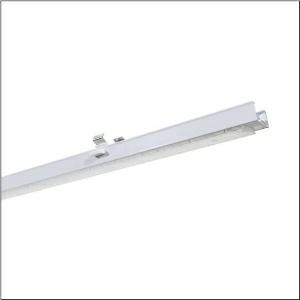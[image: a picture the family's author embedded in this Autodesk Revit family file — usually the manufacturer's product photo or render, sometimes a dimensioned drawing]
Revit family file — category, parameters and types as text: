
# Revit family: trunking_flex_31_51re12ma16b
name_source: partatom
category: Lighting Fixtures
units: mm (PartAtom-declared; Revit-internal decimal feet)

## family parameters
Cut with Voids When Loaded = No
Host = Face
Light Source = No
Part Type = Normal
Room Calculation Point = No
Round Connector Dimension = Use Diameter
Shared = No

## types (1)
- --- (1 x LED, 6400 lm, 40 W, 3500K)
    Apparent Load = 40 VA
    CIE Flux Codes = 65 91 98 99 100
    Color Rendering = 80
    Color Temperature = 3500K
    Default Elevation = 1800 mm
    Description = Trunking Flex 31, luminaire insert, of extruded aluminium section, coated, traffic white (RAL 9016), length: 1.172mm, width: 91mm, height: 53mm, LED rated luminous flux: 6.400lm, light colour: 835, control gear: ON/OFF Multilumen, with system connector: socket, mains connection: 220..240V, AC, 50/60Hz, rated input power: 40W, luminous flux adjustable on luminaire in four steps (3420/4540/5580/6630lm), connected load according to luminous flux setting (20/26/33/40W), primary light control with lens, of plastic, primary optical cover: cover, of PMMA, light emission: direct distribution, protection rating (complete): IP20, insulation class (complete): insulation class I (protective earthing), certification: CE, UKCA, impact resistance: IK02, permissible ambient temperature for indoor applications: -20..+40°C, packaging unit: 1 piece
    Height = 58 mm
    Lamp = 1 x LED
    Lamp Light Flux = 6400 lm
    Lamp Power = 40 W
    Lamp count = 1
    Length = 1172 mm
    Luminous efficacy = 160 lm/W
    Manufacturer = Siteco
    ModVariant = No
    Model = 51RE12MA16B
    Mounting Place = Ceiling
    Mounting Type = Pendant
    Number of Poles = 1
    OnlyDefault = Yes
    Power Factor = 1
    Product Name = Trunking Flex 31
    Product group = luminaire insert
    ProductGroupID = 902
    Protection Class = Protection class I
    Protection Degree = IP 20
    RLX_Detail_Level = 1
    RLX_Emergency_Light_Flux = 0 lm
    RLX_Emergency_Type = 0
    RLX_Emergency_Type_DB = No
    RlxData = <blob elided: 19949 chars, md5=12f4be28>
    Socket = socket
    Standby Power = 0 W
    System Light Flux = 6400 lm
    System Power = 40 W
    Type Comments = factory setting: luminous flux: 100 % | (ON | ON) | 300 mA
    Type Image = l_1266702.jpg
    URL = http://relux.com
    VarID = @adj_059198
    Voltage = 0 V
    Weight = 0.00 kg
    Width = 65 mm

## geometry (parser evidence)
native form markers: Blend x4, Sweep x10
no freeform markers — native parametric forms only
